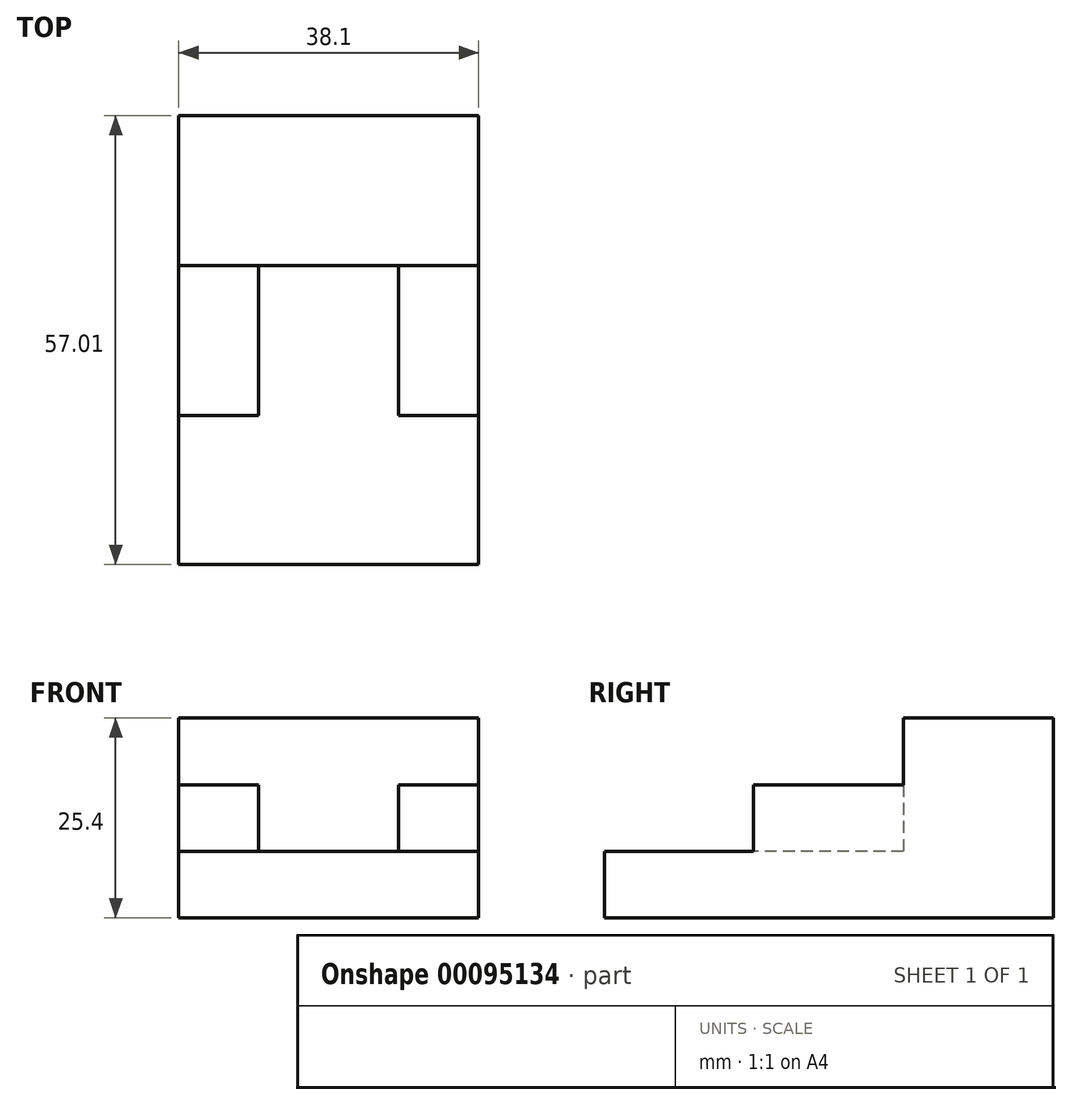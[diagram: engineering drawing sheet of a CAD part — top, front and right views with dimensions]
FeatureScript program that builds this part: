
annotation { "Feature Type Name" : "Feature", "Feature Type Description" : "" }
export const myFeature = defineFeature(function(context is Context, id is Id, definition is map)
    precondition{}
    {
        {
            var Q0;
            Q0=qCreatedBy(makeId("Top.planeOp"),FACE);
            var sketch = newSketch(context, id + "F0", { "sketchPlane" : qUnion([Q0])});
            skLineSegment(sketch, "E0.bottom", {"start": v(19.05, 9.52) * mm, "end": v(-19.05, 9.52) * mm});
            skLineSegment(sketch, "E0.top", {"start": v(19.05, -9.53) * mm, "end": v(-19.05, -9.53) * mm});
            skLineSegment(sketch, "E0.left", {"start": v(19.05, 9.52) * mm, "end": v(19.05, -9.53) * mm});
            skLineSegment(sketch, "E0.right", {"start": v(-19.05, 9.52) * mm, "end": v(-19.05, -9.53) * mm});
            skPoint(sketch, "E0.middle", {"position": v(0, 0) * mm});
            skSolve(sketch);
        }
        {
            var Q0;
            Q0=makeQuery(id+"F0.imprint","IMPRINT",FACE,{"disambiguationData":[TD([[makeQuery(id+"F0.imprint","IMPRINT",EDGE,{"derivedFrom":sQuery(id+"F0.wireOp",EDGE,"E0.bottom")}),1.0]])]});
            extrude(context, id + "F1", {"entities" : qUnion([Q0]), "depth" : 25.4 * mm});
        }
        {
            var Q0;
            Q0=qCreatedBy(makeId("Top.planeOp"),FACE);
            var sketch = newSketch(context, id + "F2", { "sketchPlane" : qUnion([Q0])});
            skLineSegment(sketch, "E1.bottom", {"start": v(-19.05, -9.38) * mm, "end": v(19.05, -9.38) * mm});
            skLineSegment(sketch, "E1.top", {"start": v(-19.05, -47.48) * mm, "end": v(19.05, -47.48) * mm});
            skLineSegment(sketch, "E1.left", {"start": v(-19.05, -9.38) * mm, "end": v(-19.05, -47.48) * mm});
            skLineSegment(sketch, "E1.right", {"start": v(19.05, -9.38) * mm, "end": v(19.05, -47.48) * mm});
            skSolve(sketch);
        }
        {
            var Q0;
            Q0=makeQuery(id+"F2.imprint","IMPRINT",FACE,{"disambiguationData":[TD([[makeQuery(id+"F2.imprint","IMPRINT",EDGE,{"derivedFrom":sQuery(id+"F2.wireOp",EDGE,"E1.bottom")}),-1.0]])]});
            extrude(context, id + "F3", {"entities" : qUnion([Q0]), "operationType" : NewBodyOperationType.ADD, "depth" : 8.43 * mm});
        }
        {
            var Q0;
            Q0=makeQuery(id+"F3.opExtrude","CAP_FACE",FACE,{"disambiguationData":[OSD([sQuery(id+"F2.wireOp",EDGE,"E1.bottom"),sQuery(id+"F2.wireOp",EDGE,"E1.top"),sQuery(id+"F2.wireOp",EDGE,"E1.left"),sQuery(id+"F2.wireOp",EDGE,"E1.right")])],"isStart":false});
            var sketch = newSketch(context, id + "F4", { "sketchPlane" : qUnion([Q0])});
            skLineSegment(sketch, "E2.bottom", {"start": v(-19.05, -9.53) * mm, "end": v(-8.9, -9.53) * mm});
            skLineSegment(sketch, "E2.top", {"start": v(-19.05, -28.58) * mm, "end": v(-8.9, -28.58) * mm});
            skLineSegment(sketch, "E2.left", {"start": v(-19.05, -9.53) * mm, "end": v(-19.05, -28.58) * mm});
            skLineSegment(sketch, "E2.right", {"start": v(-8.9, -9.53) * mm, "end": v(-8.9, -28.58) * mm});
            skLineSegment(sketch, "E3.bottom", {"start": v(19.05, -9.53) * mm, "end": v(8.89, -9.53) * mm});
            skLineSegment(sketch, "E3.top", {"start": v(19.05, -28.58) * mm, "end": v(8.9, -28.58) * mm});
            skLineSegment(sketch, "E3.left", {"start": v(19.05, -9.53) * mm, "end": v(19.05, -28.58) * mm});
            skLineSegment(sketch, "E3.right", {"start": v(8.89, -9.53) * mm, "end": v(8.9, -28.58) * mm});
            skSolve(sketch);
        }
        {
            var Q0;
            Q0=makeQuery(id+"F4.imprint","IMPRINT",FACE,{"disambiguationData":[TD([[makeQuery(id+"F4.imprint","IMPRINT",EDGE,{"derivedFrom":sQuery(id+"F4.wireOp",EDGE,"E2.bottom")}),1.0]])]});
            extrude(context, id + "F5", {"entities" : qUnion([Q0]), "operationType" : NewBodyOperationType.ADD, "depth" : 8.46 * mm});
        }
        {
            var Q0;
            Q0=makeQuery(id+"F4.imprint","IMPRINT",FACE,{"disambiguationData":[TD([[makeQuery(id+"F4.imprint","IMPRINT",EDGE,{"derivedFrom":sQuery(id+"F4.wireOp",EDGE,"E3.bottom")}),1.0]])]});
            extrude(context, id + "F6", {"entities" : qUnion([Q0]), "operationType" : NewBodyOperationType.ADD, "depth" : 8.46 * mm});
        }
    });
